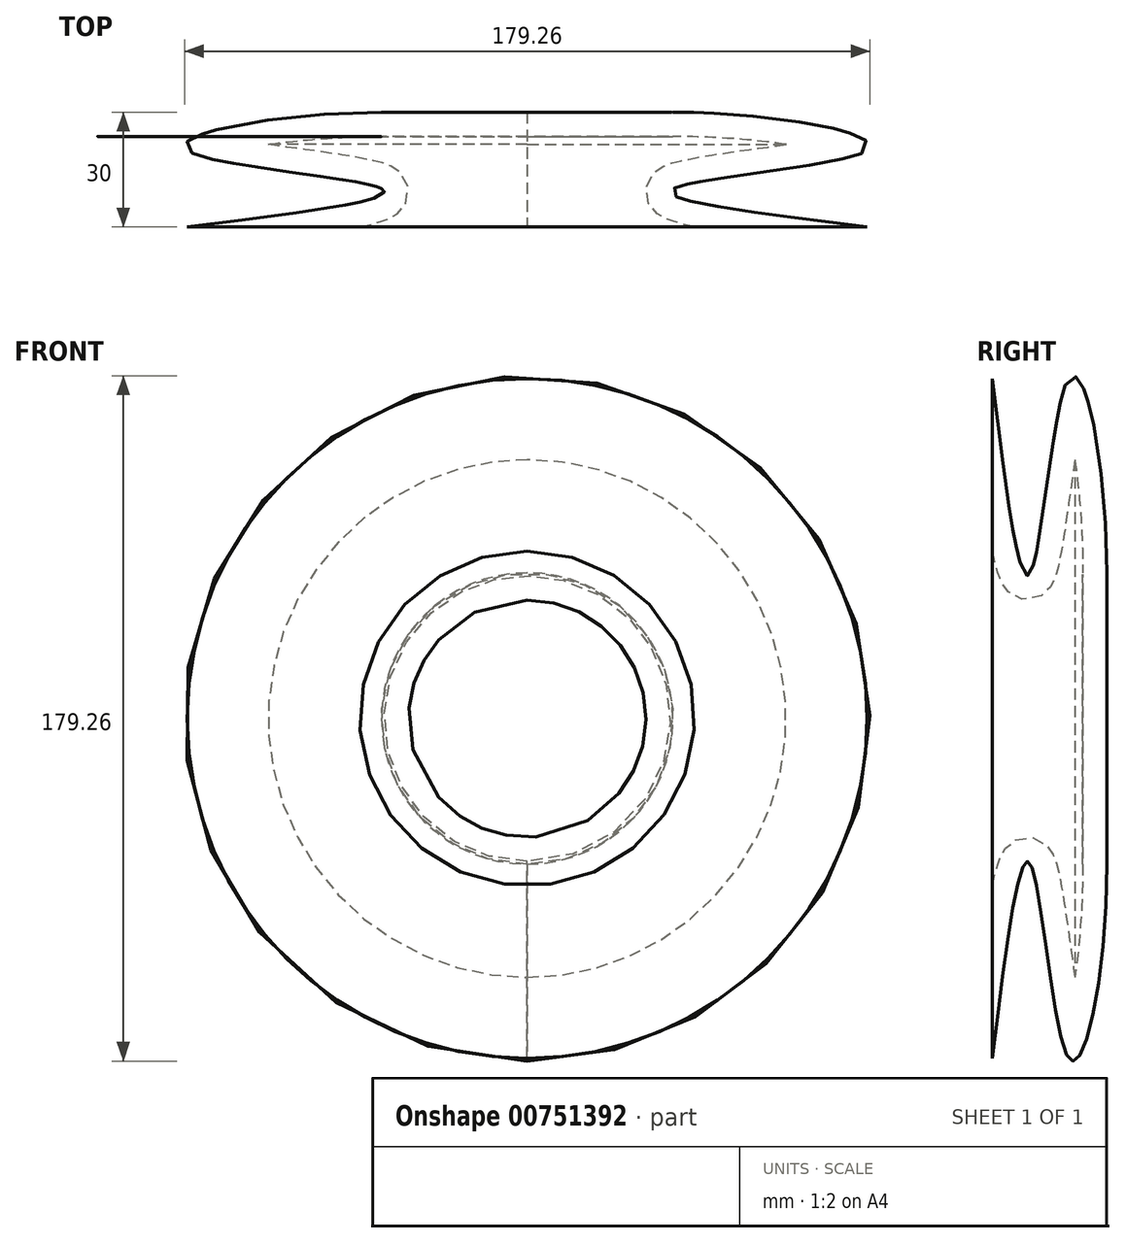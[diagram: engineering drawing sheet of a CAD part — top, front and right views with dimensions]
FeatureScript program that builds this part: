
annotation { "Feature Type Name" : "Feature", "Feature Type Description" : "" }
export const myFeature = defineFeature(function(context is Context, id is Id, definition is map)
    precondition{}
    {
        {
            assignVariable(context, id + "F0", {"name" : "offsetDistance", "anyValue" : 10});
        }
        {
            var Q0;
            Q0=qCreatedBy(makeId("Front.planeOp"),FACE);
            var sketch = newSketch(context, id + "F1", { "sketchPlane" : qUnion([Q0])});
            skCircle(sketch, "E0", {"center": v(0, 0) * mm, "radius": 38.1 * mm});
            skSolve(sketch);
        }
        {
            var Q0;
            Q0=makeQuery(id+"F1.imprint","IMPRINT",FACE,{"disambiguationData":[TD([[makeQuery(id+"F1.imprint","IMPRINT",EDGE,{"derivedFrom":sQuery(id+"F1.wireOp",EDGE,"E0")}),1.0]])]});
            cPlane(context, id + "F2", {"entities" : qUnion([Q0]), "cplaneType" : CPlaneType.OFFSET, "offset" : (getVariable(context, 'offsetDistance')) * mm, "width" : 152.4 * mm, "height" : 152.4 * mm});
        }
        {
            var Q0;
            Q0=qCreatedBy(id+"F2.planeOp",FACE);
            var sketch = newSketch(context, id + "F3", { "sketchPlane" : qUnion([Q0])});
            skCircle(sketch, "E1", {"center": v(0, 0) * mm, "radius": 88.9 * mm});
            skSolve(sketch);
        }
        {
            var Q0;
            Q0=makeQuery(id+"F3.imprint","IMPRINT",FACE,{"disambiguationData":[TD([[makeQuery(id+"F3.imprint","IMPRINT",EDGE,{"derivedFrom":sQuery(id+"F3.wireOp",EDGE,"E1")}),1.0]])]});
            cPlane(context, id + "F4", {"entities" : qUnion([Q0]), "cplaneType" : CPlaneType.OFFSET, "offset" : (getVariable(context, 'offsetDistance')) * mm, "width" : 152.4 * mm, "height" : 152.4 * mm});
        }
        {
            var Q0;
            Q0=qCreatedBy(id+"F4.planeOp",FACE);
            var sketch = newSketch(context, id + "F5", { "sketchPlane" : qUnion([Q0])});
            skCircle(sketch, "E2", {"center": v(0, 0) * mm, "radius": 38.1 * mm});
            skSolve(sketch);
        }
        {
            var Q0;
            Q0=qCreatedBy(id+"F4.planeOp",FACE);
            cPlane(context, id + "F6", {"entities" : qUnion([Q0]), "cplaneType" : CPlaneType.OFFSET, "offset" : (getVariable(context, 'offsetDistance')) * mm, "width" : 152.4 * mm, "height" : 152.4 * mm});
        }
        {
            var Q0;
            Q0=qCreatedBy(id+"F6.planeOp",FACE);
            var sketch = newSketch(context, id + "F7", { "sketchPlane" : qUnion([Q0])});
            skCircle(sketch, "E3", {"center": v(0, 0) * mm, "radius": 88.9 * mm});
            skSolve(sketch);
        }
        {
            var Q0;
            Q0=makeQuery(id+"F1.imprint","IMPRINT",FACE,{"disambiguationData":[TD([[makeQuery(id+"F1.imprint","IMPRINT",EDGE,{"derivedFrom":sQuery(id+"F1.wireOp",EDGE,"E0")}),1.0]])]});
            var Q1;
            Q1=makeQuery(id+"F3.imprint","IMPRINT",FACE,{"disambiguationData":[TD([[makeQuery(id+"F3.imprint","IMPRINT",EDGE,{"derivedFrom":sQuery(id+"F3.wireOp",EDGE,"E1")}),1.0]])]});
            var Q2;
            Q2=makeQuery(id+"F5.imprint","IMPRINT",FACE,{"disambiguationData":[TD([[makeQuery(id+"F5.imprint","IMPRINT",EDGE,{"derivedFrom":sQuery(id+"F5.wireOp",EDGE,"E2")}),1.0]])]});
            var Q3;
            Q3=makeQuery(id+"F7.imprint","IMPRINT",FACE,{"disambiguationData":[TD([[makeQuery(id+"F7.imprint","IMPRINT",EDGE,{"derivedFrom":sQuery(id+"F7.wireOp",EDGE,"E3")}),1.0]])]});
            loft(context, id + "F8", {"startCondition" : LoftEndDerivativeType.TANGENT_TO_PROFILE, "startMagnitude" : 1, "sheetProfilesArray" : [{ "sheetProfileEntities" : qUnion([Q0]) }, { "sheetProfileEntities" : qUnion([Q1]) }, { "sheetProfileEntities" : qUnion([Q2]) }, { "sheetProfileEntities" : qUnion([Q3]) }]});
        }
        {
            var Q0;
            Q0=makeQuery(id+"F8.opLoft","CAP_FACE",FACE,{"disambiguationData":[OSD([makeQuery(id+"F7.imprint","IMPRINT",FACE,{"disambiguationData":[TD([[makeQuery(id+"F7.imprint","IMPRINT",EDGE,{"derivedFrom":sQuery(id+"F7.wireOp",EDGE,"E3")}),1.0]])]})])],"isStart":true});
            shell(context, id + "F9", {"entities" : qUnion([Q0]), "thickness" : 6.35 * mm});
        }
    });
